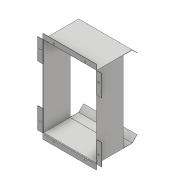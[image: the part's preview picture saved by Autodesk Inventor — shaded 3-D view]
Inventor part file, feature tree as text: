
AUTODESK INVENTOR PART (.ipt)
format: ipt  version: 2017 (Build 210142000, 142)  size: 198,144 bytes
history: native  units: mm
features: sketch x6, extrude x5, fillet x1, hole x1
ambient origin geometry x8: Origin, YZ Plane, XZ Plane, XY Plane, X Axis, Y Axis, Z Axis, Center Point
bodies: Solid1 (feature_tree)
feature tree (13):
  extrude  "Extrusion1"  Depth=228.0mm
  extrude  "Extrusion3"  Depth=15.0mm TaperAngle=0.0deg
  fillet  "Fillet1"  Radius=15.0mm
  hole  "Hole1"  [1 undecoded]
  extrude  "Extrusion7"  Depth=0.8mm TaperAngle=0.0deg
  extrude  "Extrusion8"  Depth=2.0mm
  extrude  "Extrusion9"  Depth=60.0mm
  sketch  "Sketch1"  dims[d0=150.0mm d1=228.0mm]
  sketch  "Sketch3"  dims[d2=0.8mm d3=101.6mm d4=0.0mm d11=15.0mm]
  sketch  "Sketch4"  dims[d12=15.0mm d13=15.0mm]
  sketch  "Sketch8"  dims[d14=15.0mm d15=0.8mm d16=0.0mm]
  sketch  "Sketch9"  dims[d17=2.0mm d18=164.5mm]
  sketch  "Sketch10"  dims[d19=241.3mm d20=88.9mm d21=60.0mm d22=90.0deg d23=88.9mm d24=88.9mm d25=4.496mm d26=6.0mm d27=8.433mm d28=2.0mm d29=14.3117mm d30=8.0mm d31=20.594885mm d48=25.4mm d49=1.2mm d50=0.0mm d51=20.0mm d52=45.0deg d53=20.0mm d54=135.0deg d55=1.2mm d56=0.0mm d57=60.0mm d58=60.0mm d59=0.0mm d60=0.0mm]
note: 1 required parameter value undecoded (feature->parameter linkage not recoverable at this tier; creation-order binding heuristic only, values carry confidence <= 0.55)
